FCSTD DOCUMENT  (FreeCAD 0.15R4671 (Git))
Label: Patron
License: All rights reserved
LicenseURL: http://en.wikipedia.org/wiki/All_rights_reserved
objects: Sketcher::SketchObject×1
note: 1 computed .brp shape members not serialized (recipe doc carries the construction recipe); baked Part::Feature solids carry a one-line shape summary decoded from their .brp

FEATURE [Sketcher::SketchObject] Sketch
  Placement = pos=(0,0,0) rot=(1,0,0;1.5708rad)
  sketch-geometry (14):
    g0: Circle [constr] CenterX=0 CenterY=45 CenterZ=0 NormalX=0 NormalY=0 NormalZ=1 Radius=35
    g1: LineSegment [constr] StartX=-88 StartY=0 StartZ=0 EndX=88 EndY=0 EndZ=0
    g2: LineSegment [constr] StartX=88 StartY=0 StartZ=0 EndX=88 EndY=8 EndZ=0
    g3: LineSegment [constr] StartX=88 StartY=8 StartZ=0 EndX=-88 EndY=8 EndZ=0
    g4: LineSegment [constr] StartX=-88 StartY=8 StartZ=0 EndX=-88 EndY=0 EndZ=0
    g5: LineSegment StartX=-90 StartY=0 StartZ=0 EndX=-80 EndY=0 EndZ=0
    g6: LineSegment StartX=-80 StartY=0 StartZ=0 EndX=-80 EndY=-12 EndZ=0
    g7: LineSegment StartX=-80 StartY=-12 StartZ=0 EndX=-105 EndY=-12 EndZ=0
    g8: LineSegment StartX=-105 StartY=-12 StartZ=0 EndX=-105 EndY=0 EndZ=0
    g9: GeomPoint [constr] X=0 Y=150 Z=0
    g10: LineSegment StartX=90 StartY=0 StartZ=0 EndX=80 EndY=0 EndZ=0
    g11: LineSegment StartX=80 StartY=0 StartZ=0 EndX=80 EndY=-12 EndZ=0
    g12: LineSegment StartX=80 StartY=-12 StartZ=0 EndX=105 EndY=-12 EndZ=0
    g13: LineSegment StartX=105 StartY=-12 StartZ=0 EndX=105 EndY=0 EndZ=0
  constraints (41):
    c: PointOnObject(g0,g-2)
    c: Radius(g0) = 35
    c: DistanceY(g-1,g0) = 45
    c: Coincident(g1,g2)
    c: Coincident(g2,g3)
    c: Coincident(g3,g4)
    c: Coincident(g4,g1)
    c: Horizontal(g3)
    c: Vertical(g2)
    c: Vertical(g4)
    c: PointOnObject(g1,g-1)
    c: Distance(g4) = 8
    c: Symmetric(g1,g1,g-2)
    c: Distance(g3) = 176
    c: PointOnObject(g5,g-1)
    c: PointOnObject(g5,g1)
    c: Coincident(g5,g6)
    c: Vertical(g6)
    c: Coincident(g6,g7)
    c: Horizontal(g7)
    c: Distance(g6) = 12
    c: Coincident(g8,g7)
    c: PointOnObject(g8,g-1)
    c: Vertical(g8)
    c: DistanceX(g-1,g5) = -90
    c: Distance(g5) = 10
    c: DistanceX(g-1,g8) = -105
    c: PointOnObject(g9,g-2)
    c: DistanceY(g-1,g9) = 150
    c: Horizontal(g10)
    c: Coincident(g10,g11)
    c: Vertical(g11)
    c: Coincident(g11,g12)
    c: Horizontal(g12)
    c: Coincident(g12,g13)
    c: PointOnObject(g13,g-1)
    c: Vertical(g13)
    c: Symmetric(g5,g10,g-2)
    c: Symmetric(g10,g5,g-2)
    c: Symmetric(g8,g13,g-2)
    c: Symmetric(g6,g11,g-2)
